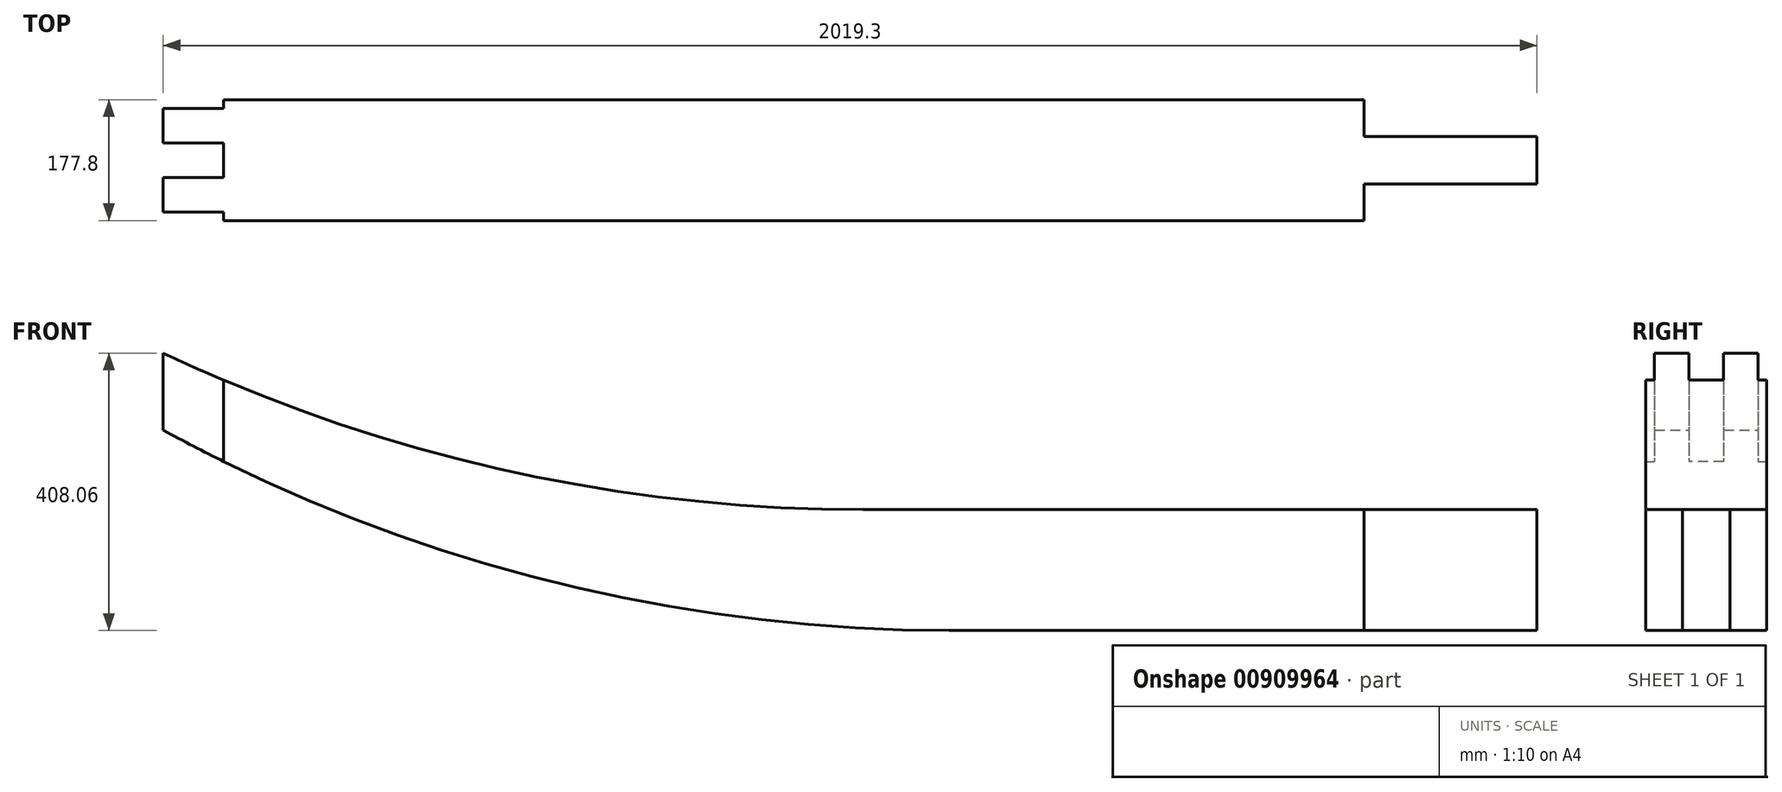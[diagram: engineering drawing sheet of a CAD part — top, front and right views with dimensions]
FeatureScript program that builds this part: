
annotation { "Feature Type Name" : "Feature", "Feature Type Description" : "" }
export const myFeature = defineFeature(function(context is Context, id is Id, definition is map)
    precondition{}
    {
        {
            var Q0;
            Q0=qCreatedBy(makeId("Front.planeOp"),FACE);
            var sketch = newSketch(context, id + "F0", { "sketchPlane" : qUnion([Q0])});
            skLineSegment(sketch, "E0.bottom", {"start": v(-127, 0) * mm, "end": v(609.6, 0) * mm});
            skLineSegment(sketch, "E0.top", {"start": v(0, -177.8) * mm, "end": v(609.6, -177.8) * mm});
            skLineSegment(sketch, "E0.right", {"start": v(609.6, 0) * mm, "end": v(609.6, -177.8) * mm});
            skArc(sketch, "E1", {"start": v(-1155.7, 230.26) * mm, "mid": v(-654.08, 58.27) * mm, "end": v(-127, 0) * mm});
            skArc(sketch, "E2", {"start": v(-1155.7, 116.96) * mm, "mid": v(-596.35, -102.95) * mm, "end": v(0, -177.8) * mm});
            skLineSegment(sketch, "E3", {"start": v(-1155.7, 230.26) * mm, "end": v(-1155.7, 116.96) * mm});
            skLineSegment(sketch, "E4", {"start": v(609.6, 0) * mm, "end": v(863.6, 0) * mm});
            skLineSegment(sketch, "E5", {"start": v(863.6, 0) * mm, "end": v(863.6, -177.8) * mm});
            skLineSegment(sketch, "E6", {"start": v(863.6, -177.8) * mm, "end": v(609.6, -177.8) * mm});
            skLineSegment(sketch, "E7", {"start": v(-1066.8, 190.54) * mm, "end": v(-1066.8, 70.83) * mm});
            skSolve(sketch);
        }
        {
            var Q0;
            Q0=makeQuery(id+"F0.imprint","IMPRINT",FACE,{"disambiguationData":[TD([[makeQuery(id+"F0.imprint","IMPRINT",EDGE,{"derivedFrom":sQuery(id+"F0.wireOp",EDGE,"E0.right")}),1.0]])]});
            extrude(context, id + "F1", {"entities" : qUnion([Q0]), "flatOperationType" : FlatOperationType.REMOVE, "depth" : 69.85 * mm, "offsetDistance" : 25 * mm, "domain" : OperationDomain.MODEL, "symmetric" : true});
        }
        {
            var Q0;
            {var subQ1=sQuery(id+"F0.wireOp",EDGE,"E0.bottom");Q0=makeQuery(id+"F0.imprint","IMPRINT",FACE,{"disambiguationData":[TD([[makeQuery(id+"F0.imprint","IMPRINT",EDGE,{"derivedFrom":subQ1}),-1.0]])]});}
            extrude(context, id + "F2", {"entities" : qUnion([Q0]), "operationType" : NewBodyOperationType.ADD, "flatOperationType" : FlatOperationType.REMOVE, "depth" : 177.8 * mm, "offsetDistance" : 25 * mm, "domain" : OperationDomain.MODEL, "symmetric" : true});
        }
        {
            var Q0;
            {var subQ0=sQuery(id+"F0.wireOp",EDGE,"E3");Q0=makeQuery(id+"F0.imprint","IMPRINT",FACE,{"disambiguationData":[TD([[makeQuery(id+"F0.imprint","IMPRINT",EDGE,{"derivedFrom":subQ0}),1.0]])]});}
            extrude(context, id + "F3", {"entities" : qUnion([Q0]), "operationType" : NewBodyOperationType.ADD, "flatOperationType" : FlatOperationType.REMOVE, "depth" : 152.4 * mm, "offsetDistance" : 25 * mm, "domain" : OperationDomain.MODEL, "symmetric" : true});
        }
        {
            var Q0;
            {var subQ0=sQuery(id+"F0.wireOp",EDGE,"E3");Q0=makeQuery(id+"F0.imprint","IMPRINT",FACE,{"disambiguationData":[TD([[makeQuery(id+"F0.imprint","IMPRINT",EDGE,{"derivedFrom":subQ0}),1.0]])]});}
            extrude(context, id + "F4", {"entities" : qUnion([Q0]), "operationType" : NewBodyOperationType.REMOVE, "flatOperationType" : FlatOperationType.REMOVE, "oppositeDirection" : true, "depth" : 50.8 * mm, "offsetDistance" : 25 * mm, "domain" : OperationDomain.MODEL, "symmetric" : true});
        }
    });
